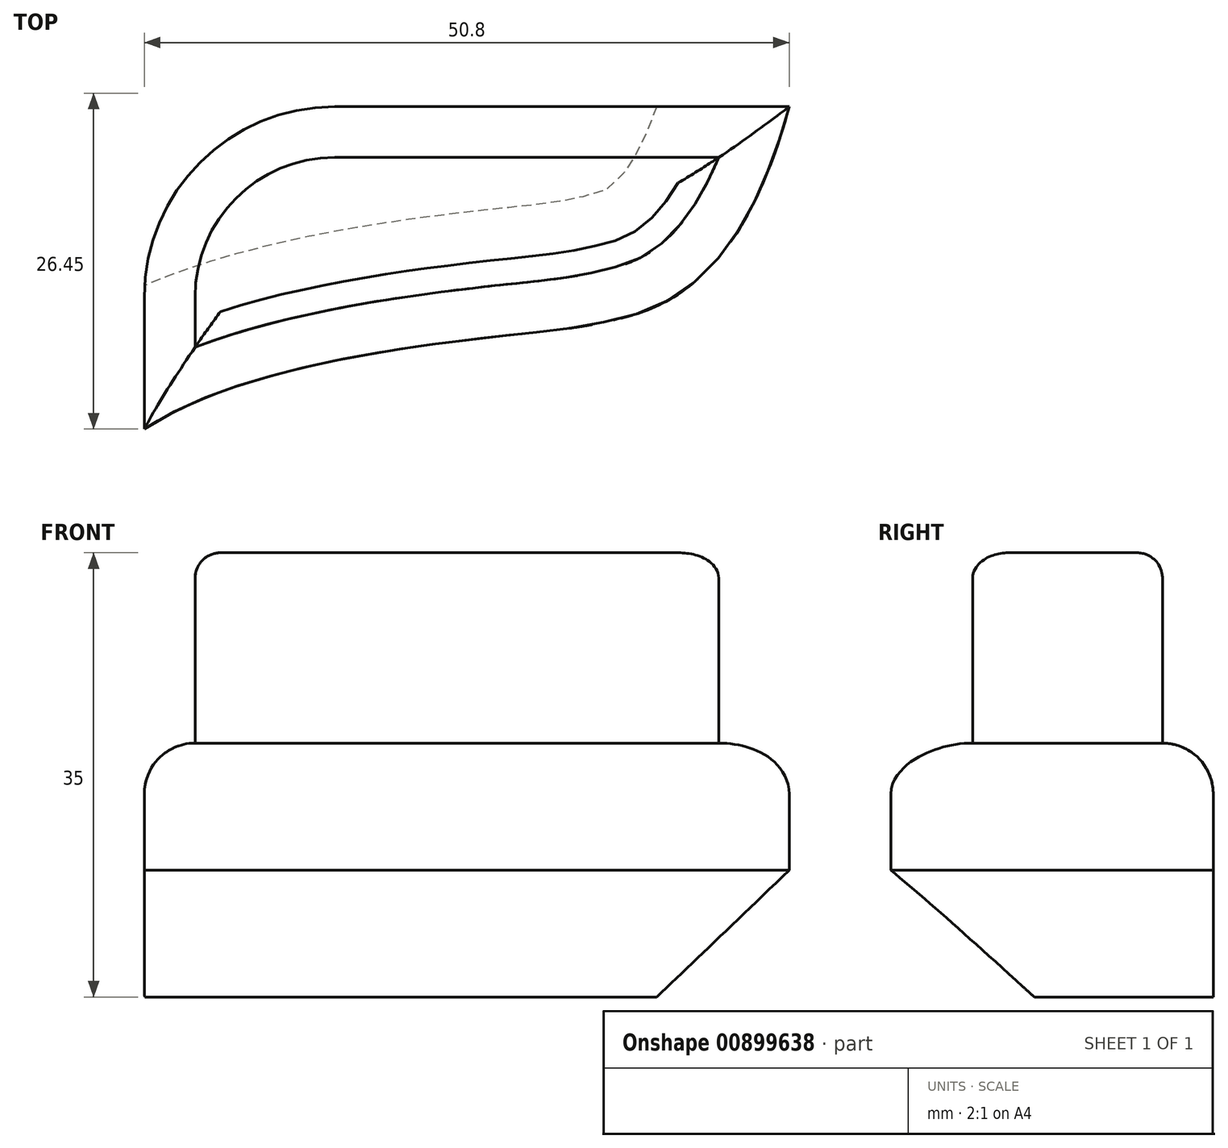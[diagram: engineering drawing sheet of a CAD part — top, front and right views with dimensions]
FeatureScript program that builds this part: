
annotation { "Feature Type Name" : "Feature", "Feature Type Description" : "" }
export const myFeature = defineFeature(function(context is Context, id is Id, definition is map)
    precondition{}
    {
        {
            var Q0;
            Q0=qCreatedBy(makeId("Top.planeOp"),FACE);
            var sketch = newSketch(context, id + "F0", { "sketchPlane" : qUnion([Q0])});
            skLineSegment(sketch, "E0", {"start": v(15, 0) * mm, "end": v(50.8, 0) * mm});
            skLineSegment(sketch, "E1", {"start": v(0, -15) * mm, "end": v(0, -25.4) * mm});
            skFitSpline(sketch, "E2", {"points": [v(50.8, 0) * mm, v(37.07, -16.78) * mm, v(31.72, -17.68) * mm, v(0, -25.4) * mm], "startDerivative": vector(-31.7, -117.1) * mm, "endDerivative": vector(-56.4, -37.44) * mm});
            skPoint(sketch, "E3.visualSharp", {"position": v(0, 0) * mm});
            skArc(sketch, "E4", {"start": v(15, 0) * mm, "mid": v(4.4, -4.4) * mm, "end": v(0, -15) * mm});
            skSolve(sketch);
        }
        {
            var Q0;
            Q0=makeQuery(id+"F0.imprint","IMPRINT",FACE,{"disambiguationData":[TD([[makeQuery(id+"F0.imprint","IMPRINT",EDGE,{"derivedFrom":sQuery(id+"F0.wireOp",EDGE,"E0")}),-1.0]])]});
            extrude(context, id + "F1", {"entities" : qUnion([Q0]), "depth" : 20 * mm, "offsetDistance" : 25 * mm});
        }
        {
            var Q0;
            Q0=makeQuery(id+"F1.opExtrude","CAP_EDGE",EDGE,{"disambiguationData":[OSD([sQuery(id+"F0.wireOp",EDGE,"E2")])],"isStart":false});
            var Q1;
            Q1=makeQuery(id+"F1.opExtrude","CAP_FACE",FACE,{"disambiguationData":[OSD([sQuery(id+"F0.wireOp",EDGE,"E0"),sQuery(id+"F0.wireOp",EDGE,"E1"),sQuery(id+"F0.wireOp",EDGE,"E2"),sQuery(id+"F0.wireOp",EDGE,"E4")])],"isStart":false});
            fillet(context, id + "F2", {"entities" : qUnion([Q0, Q1]), "radius" : 4 * mm, "tangentPropagation" : true, "allowEdgeOverflow" : false});
        }
        {
            var Q0;
            Q0=makeQuery(id+"F1.opExtrude","CAP_EDGE",EDGE,{"disambiguationData":[OSD([sQuery(id+"F0.wireOp",EDGE,"E2")])],"isStart":true});
            chamfer(context, id + "F3", {"entities" : qUnion([Q0]), "width" : 10 * mm, "tangentPropagation" : true});
        }
        {
            var Q0;
            Q0=makeQuery(id+"F1.opExtrude","CAP_FACE",FACE,{"disambiguationData":[OSD([sQuery(id+"F0.wireOp",EDGE,"E0"),sQuery(id+"F0.wireOp",EDGE,"E1"),sQuery(id+"F0.wireOp",EDGE,"E2"),sQuery(id+"F0.wireOp",EDGE,"E4")])],"isStart":false});
            extrude(context, id + "F4", {"entities" : qUnion([Q0]), "operationType" : NewBodyOperationType.ADD, "depth" : 15 * mm, "offsetDistance" : 25 * mm});
        }
        {
            var Q0;
            {var subQ0=sQuery(id+"F0.wireOp",EDGE,"E4");var subQ1=sQuery(id+"F0.wireOp",EDGE,"E2");var subQ2=sQuery(id+"F0.wireOp",EDGE,"E1");var subQ3=sQuery(id+"F0.wireOp",EDGE,"E0");Q0=makeQuery(id+"F4.opExtrude","CAP_EDGE",EDGE,{"disambiguationData":[OSD([subQ3,subQ2,subQ1,subQ0]),TDD([makeQuery(id+"F2.opFillet","BLEND_EDGE",EDGE,{"blendedFrom":[makeQuery(id+"F1.opExtrude","CAP_EDGE",EDGE,{"disambiguationData":[OSD([subQ1])],"isStart":false}),makeQuery(id+"F1.opExtrude","CAP_FACE",FACE,{"disambiguationData":[OSD([subQ3,subQ2,subQ1,subQ0])],"isStart":false})],"blendedInto":[makeQuery(id+"F1.opExtrude","CAP_FACE",FACE,{"disambiguationData":[OSD([subQ3,subQ2,subQ1,subQ0])],"isStart":false})]})])],"isStart":false});}
            var Q1;
            {var subQ0=sQuery(id+"F0.wireOp",EDGE,"E4");var subQ1=sQuery(id+"F0.wireOp",EDGE,"E2");var subQ2=sQuery(id+"F0.wireOp",EDGE,"E1");var subQ3=sQuery(id+"F0.wireOp",EDGE,"E0");Q1=makeQuery(id+"F4.opExtrude","CAP_EDGE",EDGE,{"disambiguationData":[OSD([subQ3,subQ2,subQ1,subQ0]),TDD([makeQuery(id+"F2.opFillet","BLEND_EDGE",EDGE,{"blendedFrom":[makeQuery(id+"F1.opExtrude","CAP_EDGE",EDGE,{"disambiguationData":[OSD([subQ3])],"isStart":false}),makeQuery(id+"F1.opExtrude","CAP_FACE",FACE,{"disambiguationData":[OSD([subQ3,subQ2,subQ1,subQ0])],"isStart":false})],"blendedInto":[makeQuery(id+"F1.opExtrude","CAP_FACE",FACE,{"disambiguationData":[OSD([subQ3,subQ2,subQ1,subQ0])],"isStart":false})]})])],"isStart":false});}
            var Q2;
            {var subQ0=sQuery(id+"F0.wireOp",EDGE,"E4");var subQ1=sQuery(id+"F0.wireOp",EDGE,"E2");var subQ2=sQuery(id+"F0.wireOp",EDGE,"E1");var subQ3=sQuery(id+"F0.wireOp",EDGE,"E0");Q2=makeQuery(id+"F4.opExtrude","CAP_EDGE",EDGE,{"disambiguationData":[OSD([subQ3,subQ2,subQ1,subQ0]),TDD([makeQuery(id+"F2.opFillet","BLEND_EDGE",EDGE,{"blendedFrom":[makeQuery(id+"F1.opExtrude","CAP_EDGE",EDGE,{"disambiguationData":[OSD([subQ0])],"isStart":false}),makeQuery(id+"F1.opExtrude","CAP_FACE",FACE,{"disambiguationData":[OSD([subQ3,subQ2,subQ1,subQ0])],"isStart":false})],"blendedInto":[makeQuery(id+"F1.opExtrude","CAP_FACE",FACE,{"disambiguationData":[OSD([subQ3,subQ2,subQ1,subQ0])],"isStart":false})]})])],"isStart":false});}
            fillet(context, id + "F5", {"entities" : qUnion([Q0, Q1, Q2]), "radius" : 2 * mm, "tangentPropagation" : true, "allowEdgeOverflow" : false});
        }
    });
